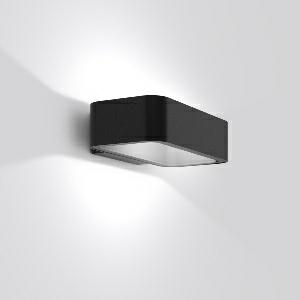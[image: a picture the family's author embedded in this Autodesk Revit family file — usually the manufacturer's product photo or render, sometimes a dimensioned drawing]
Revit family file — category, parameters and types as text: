
# Revit family: hb_103_611982_0031_c3b4
name_source: partatom
category: Lighting Fixtures
units: mm (PartAtom-declared; Revit-internal decimal feet)

## family parameters
Cut with Voids When Loaded = No
Host = Face
Light Source = No
Part Type = Normal
Room Calculation Point = No
Round Connector Dimension = Use Diameter
Shared = No

## types (1)
- HB 103 (1 x LED Modul 830, 300 lm, 3000)
    Apparent Load = 9 VA
    CIE Flux Codes = 19 56 97 49 100
    Color Rendering = 80
    Color Temperature = 3000
    Default Elevation = 1800 mm
    Description = Series: HB 103
Wall luminaire. Housing: die-cast aluminium, powder-coated. Diffuser: plastic (polycarbonate), opal. Light emission: on two sides. Driver integrated. 
Colour: anthracite metallic (DB703)
Length: 220 mm
Width: 130 mm
Height: 55 mm
Lamp: LED
System power: 9 W
Rated luminous flux: 300 lm
Luminous efficiency: 33 lm/W
Control gear: Regulated power supply
Protection class: I
Type of protection: IP 54
    Height = 55 mm
    Lamp = 1 x LED Modul 830
    Lamp Light Flux = 300 lm
    Lamp count = 1
    Length = 220 mm
    Lifetime = 50000 h
    Luminous efficacy = 33 lm/W
    Manufacturer = RZB
    ModVariant = No
    Model = 611982.0031
    Mounting Place = Wall
    Mounting Type = Surface mounted
    Number of Poles = 1
    OnlyDefault = Yes
    Power Factor = 1
    Product Name = HB 103
    Product group = Surface mounted Wall luminaires
    ProductGroupID = 2001
    Protection Class = Protection class I
    Protection Degree = IP 54
    RLX_Detail_Level = 1
    RLX_Emergency_Light_Flux = 0 lm
    RLX_Emergency_Type = 0
    RLX_Emergency_Type_DB = No
    RlxData = <blob elided: 61909 chars, md5=fd927665>
    Socket = socket
    Standby Power = 0 W
    System Light Flux = 300 lm
    System Power = 9 W
    Type Comments = Product without accessories
    Type Image = 611982.0031.jpg
    URL = http://relux.com
    VarID = ---
    Voltage = 0 V
    Weight = 0.00 kg
    Width = 130 mm

## geometry (parser evidence)
native form markers: Blend x4, Sweep x14
no freeform markers — native parametric forms only
